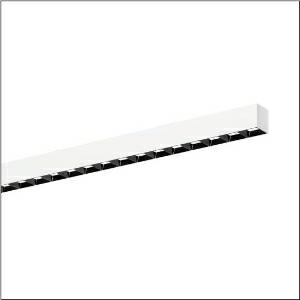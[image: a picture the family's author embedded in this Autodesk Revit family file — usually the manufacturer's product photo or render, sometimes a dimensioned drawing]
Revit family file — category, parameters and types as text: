
# Revit family: silica_21_51mx22da44wb
name_source: partatom
category: Lighting Fixtures
units: mm (PartAtom-declared; Revit-internal decimal feet)

## family parameters
Cut with Voids When Loaded = No
Host = Face
Light Source = No
Part Type = Normal
Room Calculation Point = No
Round Connector Dimension = Use Diameter
Shared = No

## types (1)
- --- (1 x LED, 4320 lm, 25.6 W, 4000K)
    Apparent Load = 26 VA
    CIE Flux Codes = 86 100 100 100 100
    Color Rendering = 80
    Color Temperature = 4000K
    Default Elevation = 1800 mm
    Description = Silica 21, office luminaire, primary light control with darklight reflector, of PMMA, black, CAT 2 (L<= 3000cd/m²), light emission: direct distribution, primary light characteristic: symmetric, installation type: surface-mounted, LED, rated luminous flux: 4.320lm, luminous efficacy: 169lm/W, light colour: 840, colour temperature: 4000K, control gear: DALI 2, with terminal, 3+2-pole, max. 2.5mm², mains connection: 220..240V, AC, 50/60Hz, rated input power: 25.6W, luminaire housing, of aluminium, traffic white (RAL 9016), length: 1.204mm, width: 53mm, height: 53mm, protection rating (complete): IP20, insulation class (complete): insulation class I (protective earthing), certification: CE, permissible operating ambient temperature: 0..+35°C, standard: EN 50419, packaging unit: 1 piece
    Height = 53 mm
    Lamp = 1 x LED
    Lamp Light Flux = 4320 lm
    Lamp Power = 25.6 W
    Lamp count = 1
    Length = 1204 mm
    Luminous efficacy = 169 lm/W
    Manufacturer = Siteco
    ModVariant = No
    Model = 51MX22DA44WB
    Mounting Place = Ceiling
    Mounting Type = Surface mounted
    Number of Poles = 1
    OnlyDefault = Yes
    Power Factor = 1
    Product Name = Silica 21
    Product group = office luminaire | ceiling mounted
    ProductGroupID = 301
    Protection Class = Protection class I
    Protection Degree = IP 20
    RLX_Detail_Level = 1
    RLX_Emergency_Light_Flux = 0 lm
    RLX_Emergency_Type = 0
    RLX_Emergency_Type_DB = No
    RlxData = <blob elided: 41225 chars, md5=996fb75a>
    Socket = socket
    Standby Power = 0 W
    System Light Flux = 4320 lm
    System Power = 26 W
    Type Comments = factory setting: luminous flux: 100 % | dim-lin: 254 | 367 mA
    Type Image = l_1335873.jpg
    URL = http://relux.com
    VarID = @adj_029127
    Voltage = 0 V
    Weight = 0.00 kg
    Width = 53 mm

## geometry (parser evidence)
native form markers: Blend x4, Sweep x10
no freeform markers — native parametric forms only
